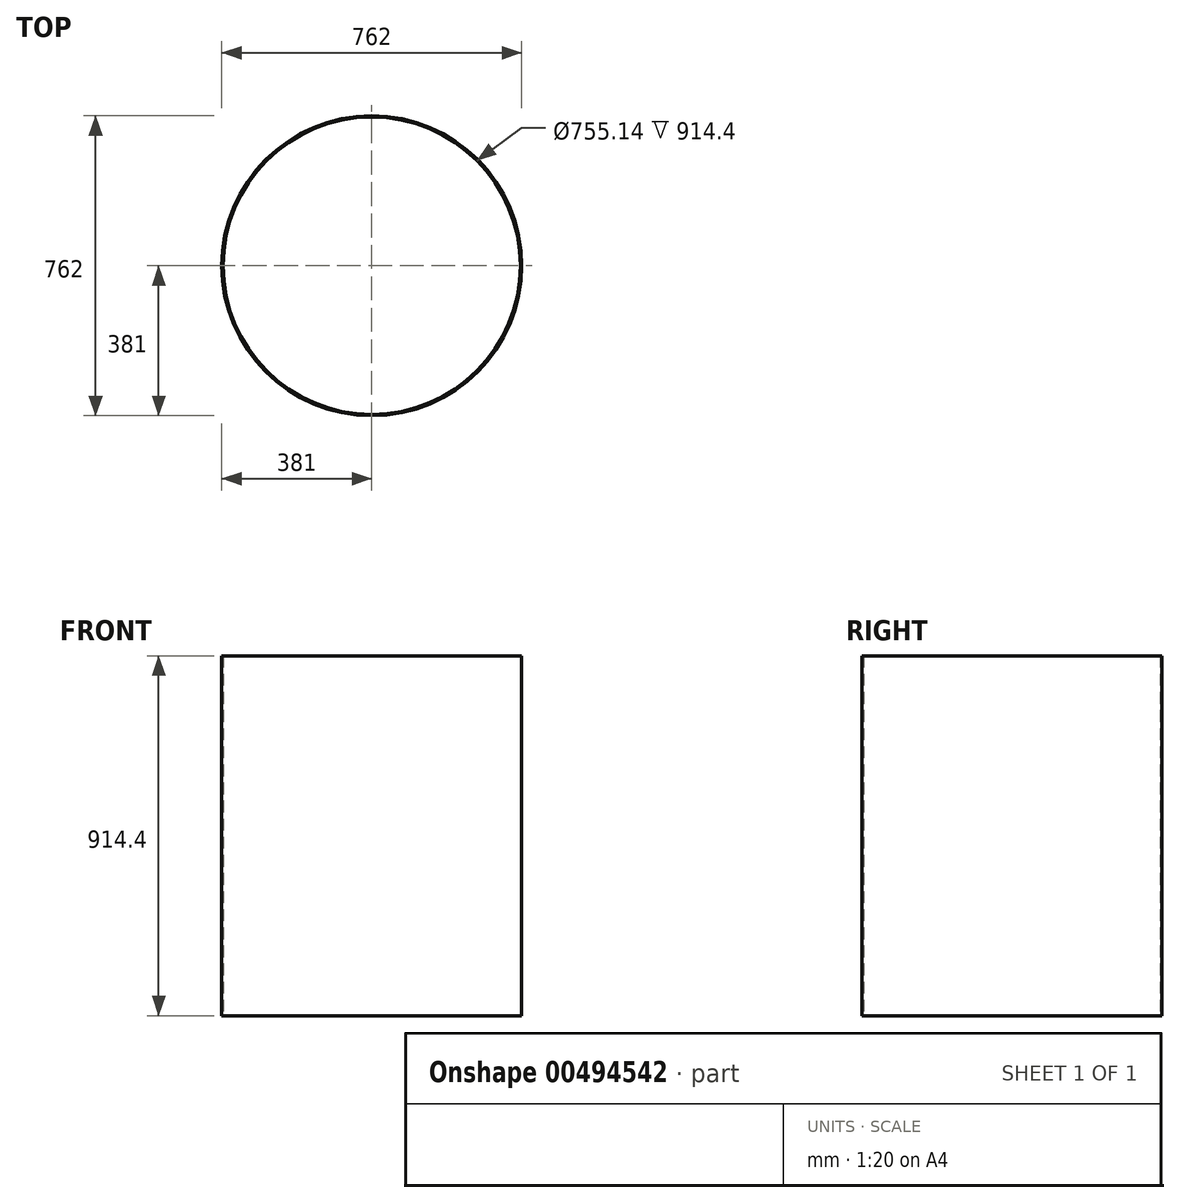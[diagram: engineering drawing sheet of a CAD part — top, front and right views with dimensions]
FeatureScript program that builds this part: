
annotation { "Feature Type Name" : "Feature", "Feature Type Description" : "" }
export const myFeature = defineFeature(function(context is Context, id is Id, definition is map)
    precondition{}
    {
        {
            var Q0;
            Q0=qCreatedBy(makeId("Top.planeOp"),FACE);
            var sketch = newSketch(context, id + "F0", { "sketchPlane" : qUnion([Q0])});
            skCircle(sketch, "E0", {"center": v(0, 0) * mm, "radius": 381 * mm});
            skCircle(sketch, "E1", {"center": v(0, 0) * mm, "radius": 377.57 * mm});
            skSolve(sketch);
        }
        {
            var Q0;
            Q0 = qSketchRegion(id + "F0", true);
            extrude(context, id + "F1", {"entities" : qUnion([Q0]), "depth" : 914.4 * mm});
        }
    });
